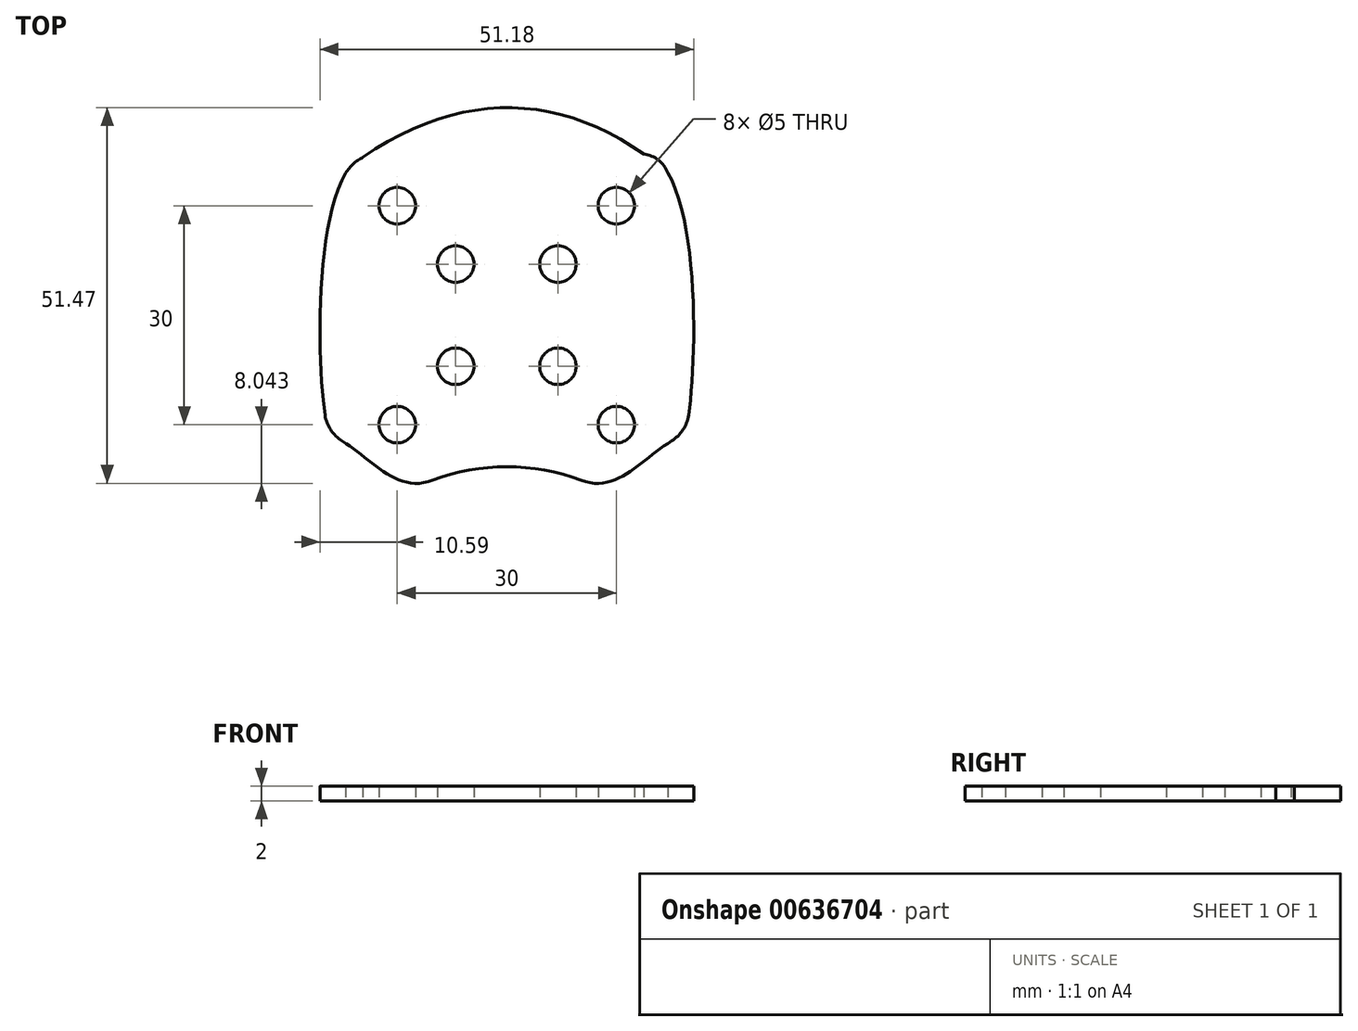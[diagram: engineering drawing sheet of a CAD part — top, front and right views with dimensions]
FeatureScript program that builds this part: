
annotation { "Feature Type Name" : "Feature", "Feature Type Description" : "" }
export const myFeature = defineFeature(function(context is Context, id is Id, definition is map)
    precondition{}
    {
        {
            var Q0;
            Q0=qCreatedBy(makeId("Top.planeOp"),FACE);
            var sketch = newSketch(context, id + "F0", { "sketchPlane" : qUnion([Q0])});
            skPoint(sketch, "E0.middle", {"position": v(3.13, -6.02) * mm});
            skPoint(sketch, "E1.middle", {"position": v(0, -0.24) * mm});
            skCircle(sketch, "E2", {"center": v(15, 14.76) * mm, "radius": 2.5 * mm});
            skCircle(sketch, "E3", {"center": v(-15, 14.76) * mm, "radius": 2.5 * mm});
            skCircle(sketch, "E4", {"center": v(-15, -15.24) * mm, "radius": 2.5 * mm});
            skPoint(sketch, "E5.visualSharp", {"position": v(-22.5, -22.74) * mm});
            skCircle(sketch, "E6.MirrorC", {"center": v(7, -7.24) * mm, "radius": 2.5 * mm});
            skCircle(sketch, "E7.MirrorC", {"center": v(-7, -7.24) * mm, "radius": 2.5 * mm});
            skCircle(sketch, "E8.MirrorC", {"center": v(-7, 6.76) * mm, "radius": 2.5 * mm});
            skCircle(sketch, "E9.MirrorC", {"center": v(7, 6.76) * mm, "radius": 2.5 * mm});
            skPoint(sketch, "E10.visualSharp", {"position": v(-22.5, 22.26) * mm});
            skArc(sketch, "E10.filletArc", {"start": v(-19.7, 21.4) * mm, "mid": v(-21.02, 20.48) * mm, "end": v(-22.05, 19.25) * mm});
            skPoint(sketch, "E11.visualSharp", {"position": v(22.5, 22.26) * mm});
            skArc(sketch, "E11.filletArc", {"start": v(22.05, 19.25) * mm, "mid": v(20.78, 21) * mm, "end": v(18.77, 21.83) * mm});
            skPoint(sketch, "E12.visualSharp", {"position": v(22.5, -22.74) * mm});
            skCircle(sketch, "E13.MirrorC", {"center": v(15, -15.24) * mm, "radius": 2.5 * mm});
            skLineSegment(sketch, "E14", {"start": v(4.24, -5.66) * mm, "end": v(4.24, -5.66) * mm});
            skLineSegment(sketch, "E15", {"start": v(4.24, -38.66) * mm, "end": v(4.24, -38.66) * mm});
            skPoint(sketch, "E16.visualSharp", {"position": v(22.05, -16.52) * mm});
            skPoint(sketch, "E17.visualSharp", {"position": v(22.05, 16.48) * mm});
            skLineSegment(sketch, "E18", {"start": v(-40.76, -5.66) * mm, "end": v(-40.76, -5.66) * mm});
            skLineSegment(sketch, "E19", {"start": v(-40.76, -38.66) * mm, "end": v(-40.76, -38.66) * mm});
            skPoint(sketch, "E20.visualSharp", {"position": v(-22.98, 16.05) * mm});
            skPoint(sketch, "E21.visualSharp", {"position": v(-22.98, -16.95) * mm});
            skPoint(sketch, "E22.visualSharp", {"position": v(-16.98, 22.05) * mm});
            skPoint(sketch, "E23.visualSharp", {"position": v(16.56, 21.44) * mm});
            skPoint(sketch, "E24.center.orphan", {"position": v(0, -22.74) * mm});
            skPoint(sketch, "E25.visualSharp", {"position": v(21.12, -19.71) * mm});
            skPoint(sketch, "E26.visualSharp", {"position": v(-22.05, -20.14) * mm});
            skArc(sketch, "E27", {"start": v(10.18, -22.87) * mm, "mid": v(0, -21.01) * mm, "end": v(-10.18, -22.87) * mm});
            skPoint(sketch, "E28.visualSharp", {"position": v(-12.35, -23.8) * mm});
            skPoint(sketch, "E29.visualSharp", {"position": v(12.35, -23.8) * mm});
            skFitSpline(sketch, "E30", {"points": [v(10.18, -22.87) * mm, v(24.17, -16.63) * mm], "startDerivative": vector(16.41, -6.18) * mm, "endDerivative": vector(14.45, 6.02) * mm});
            skFitSpline(sketch, "E31.MirrorCS", {"points": [v(-10.18, -22.87) * mm, v(-24.17, -16.63) * mm], "startDerivative": vector(-16.41, -6.18) * mm, "endDerivative": vector(-14.45, 6.02) * mm});
            skFitSpline(sketch, "E32", {"points": [v(-19.7, 21.4) * mm, v(18.77, 21.83) * mm], "startDerivative": vector(39.56, 26.95) * mm, "endDerivative": vector(36.77, -25.67) * mm});
            skFitSpline(sketch, "E33", {"points": [v(22.05, 19.25) * mm, v(24.17, -16.63) * mm], "startDerivative": vector(16.07, -27.94) * mm, "endDerivative": vector(-3.71, -2) * mm});
            skArc(sketch, "E34.filletArc", {"start": v(22.56, -17.47) * mm, "mid": v(24.12, -15.96) * mm, "end": v(24.89, -13.93) * mm});
            skArc(sketch, "E35.MirrorCS", {"start": v(-22.56, -17.47) * mm, "mid": v(-24.12, -15.96) * mm, "end": v(-24.89, -13.93) * mm});
            skFitSpline(sketch, "E36.MirrorCS", {"points": [v(-22.05, 19.25) * mm, v(-24.17, -16.63) * mm], "startDerivative": vector(-16.07, -27.94) * mm, "endDerivative": vector(3.71, -2) * mm});
            skSolve(sketch);
        }
        {
            var Q0;
            Q0=makeQuery(id+"F0.imprint","IMPRINT",FACE,{"disambiguationData":[TD([[makeQuery(id+"F0.imprint","IMPRINT",EDGE,{"derivedFrom":sQuery(id+"F0.wireOp",EDGE,"E2")}),-1.0]])]});
            extrude(context, id + "F1", {"entities" : qUnion([Q0]), "depth" : 2 * mm, "offsetDistance" : 25 * mm});
        }
    });
